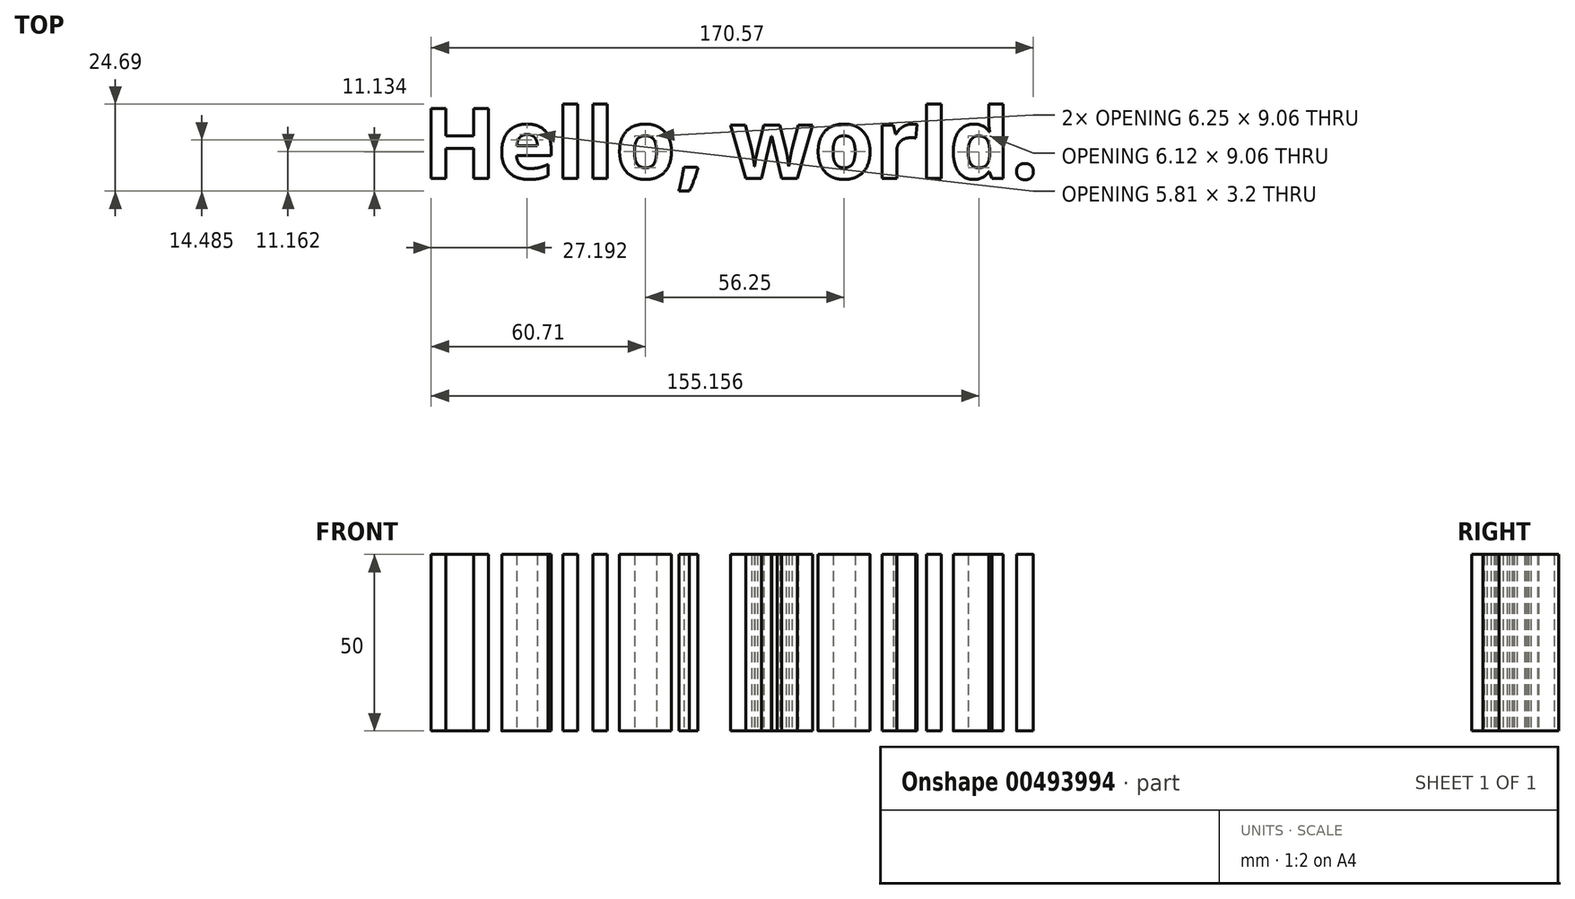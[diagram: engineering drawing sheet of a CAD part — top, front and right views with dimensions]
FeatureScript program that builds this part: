
annotation { "Feature Type Name" : "Feature", "Feature Type Description" : "" }
export const myFeature = defineFeature(function(context is Context, id is Id, definition is map)
    precondition{}
    {
        {
            var Q0;
            Q0=qCreatedBy(makeId("Top.planeOp"),FACE);
            var sketch = newSketch(context, id + "F0", { "sketchPlane" : qUnion([Q0])});
            skText(sketch, "E0", { "text": "Hello, world.", "fontName": "OpenSans-Bold.ttf"});
            const initialGuessF0  = {"E0": [-0.01603, -0.00867, 1, 0, 0.02]};
            skSetInitialGuess(sketch, initialGuessF0);
            skSolve(sketch);
        }
        {
            var Q0;
            Q0 = qSketchRegion(id + "F0", true);
            extrude(context, id + "F1", {"entities" : qUnion([Q0]), "depth" : 50 * mm});
        }
    });
